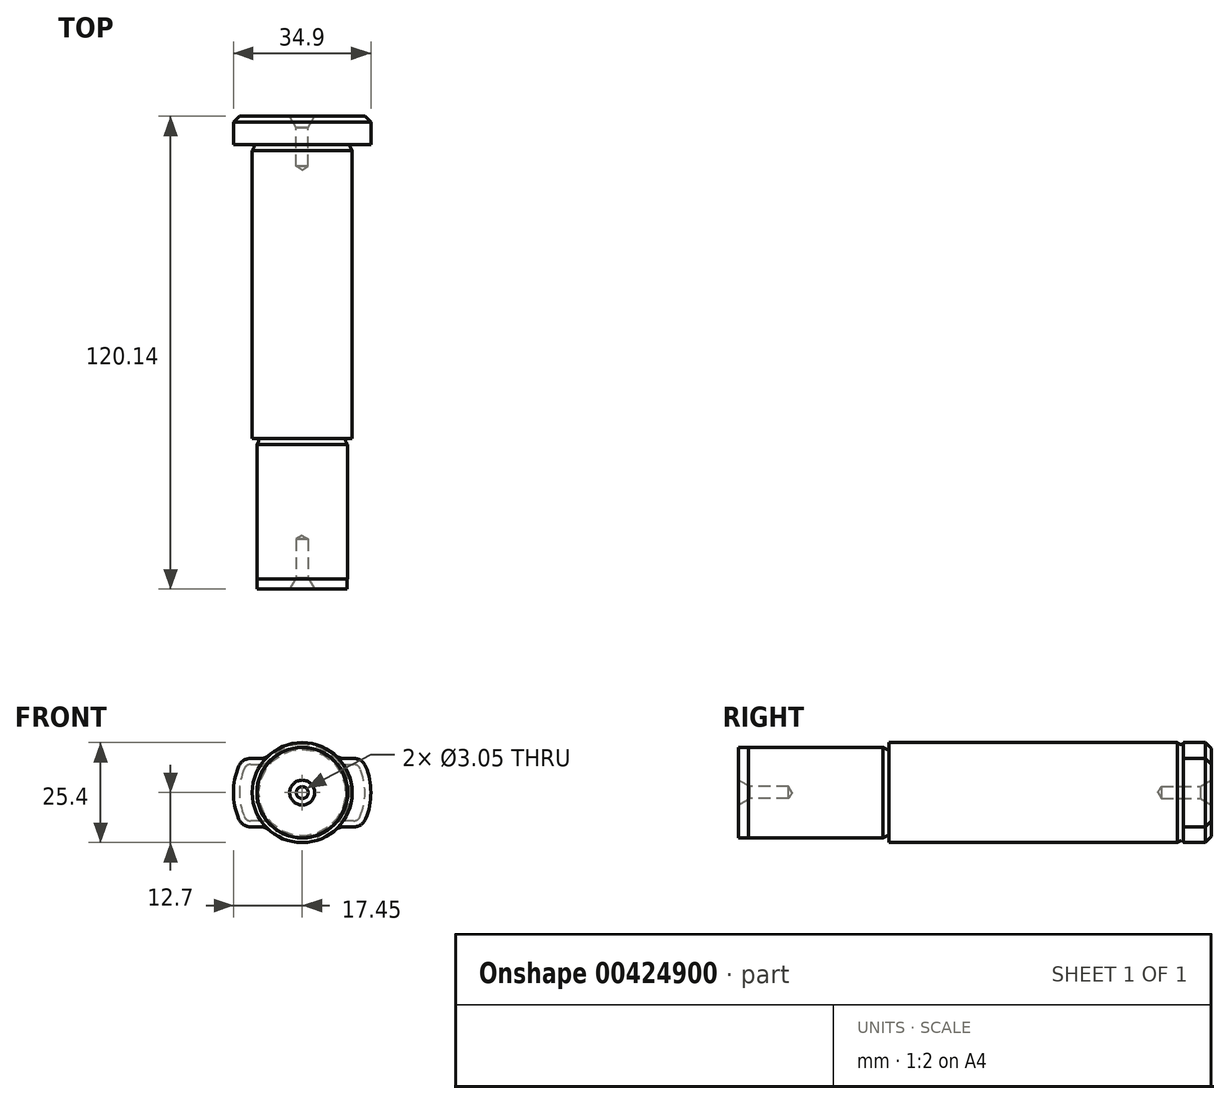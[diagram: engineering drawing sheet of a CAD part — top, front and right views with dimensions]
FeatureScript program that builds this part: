
annotation { "Feature Type Name" : "Feature", "Feature Type Description" : "" }
export const myFeature = defineFeature(function(context is Context, id is Id, definition is map)
    precondition{}
    {
        {
            var Q0;
            Q0=qCreatedBy(makeId("Front.planeOp"),FACE);
            var sketch = newSketch(context, id + "F0", { "sketchPlane" : qUnion([Q0])});
            skCircle(sketch, "E0", {"center": v(0, 0) * mm, "radius": 11.44 * mm});
            skSolve(sketch);
        }
        {
            var Q0;
            Q0 = qSketchRegion(id + "F0", true);
            extrude(context, id + "F1", {"entities" : qUnion([Q0]), "oppositeDirection" : true, "depth" : 2.54 * mm});
        }
        {
            var Q0;
            Q0=makeQuery(id+"F1.opExtrude","CAP_FACE",FACE,{"disambiguationData":[OSD([sQuery(id+"F0.wireOp",EDGE,"E0")])],"isStart":false});
            var sketch = newSketch(context, id + "F2", { "sketchPlane" : qUnion([Q0])});
            skCircle(sketch, "E1", {"center": v(0, 0) * mm, "radius": 11.52 * mm});
            skSolve(sketch);
        }
        {
            var Q0;
            Q0 = qSketchRegion(id + "F2", true);
            extrude(context, id + "F3", {"entities" : qUnion([Q0]), "operationType" : NewBodyOperationType.ADD, "depth" : 35.74 * mm});
        }
        {
            var Q0;
            Q0=makeQuery(id+"F3.opExtrude","CAP_FACE",FACE,{"disambiguationData":[OSD([sQuery(id+"F2.wireOp",EDGE,"E1")])],"isStart":false});
            var sketch = newSketch(context, id + "F4", { "sketchPlane" : qUnion([Q0])});
            skCircle(sketch, "E2", {"center": v(0, 0) * mm, "radius": 12.7 * mm});
            skSolve(sketch);
        }
        {
            var Q0;
            Q0=makeQuery(id+"F4.imprint","IMPRINT",FACE,{"disambiguationData":[TD([[makeQuery(id+"F4.imprint","IMPRINT",EDGE,{"derivedFrom":makeQuery(id+"F3.opExtrude","CAP_EDGE",EDGE,{"disambiguationData":[OSD([sQuery(id+"F2.wireOp",EDGE,"E1")])],"isStart":false})}),1.0]])]});
            var Q1;
            Q1=makeQuery(id+"F4.imprint","IMPRINT",FACE,{"disambiguationData":[TD([[makeQuery(id+"F4.imprint","IMPRINT",EDGE,{"derivedFrom":sQuery(id+"F4.wireOp",EDGE,"E2")}),1.0]])]});
            extrude(context, id + "F5", {"entities" : qUnion([Q0, Q1]), "operationType" : NewBodyOperationType.ADD, "depth" : 74.73 * mm});
        }
        {
            var Q0;
            Q0=makeQuery(id+"F5.opExtrude","CAP_FACE",FACE,{"disambiguationData":[OSD([sQuery(id+"F4.wireOp",EDGE,"E2")])],"isStart":false});
            var sketch = newSketch(context, id + "F6", { "sketchPlane" : qUnion([Q0])});
            skLineSegment(sketch, "E3.bottom", {"start": v(15.13, 8.7) * mm, "end": v(9.25, 8.7) * mm});
            skLineSegment(sketch, "E3.top", {"start": v(15.13, -8.7) * mm, "end": v(9.25, -8.7) * mm});
            skArc(sketch, "E4", {"start": v(15.13, 8.7) * mm, "mid": v(17.45, 0) * mm, "end": v(15.13, -8.7) * mm});
            skArc(sketch, "E5", {"start": v(-15.13, 8.7) * mm, "mid": v(-17.45, 0) * mm, "end": v(-15.13, -8.7) * mm});
            skArc(sketch, "E6.0", {"start": v(-9.25, -8.7) * mm, "mid": v(0, -12.7) * mm, "end": v(9.25, -8.7) * mm});
            skLineSegment(sketch, "E7.trimOffspring", {"start": v(-9.25, 8.7) * mm, "end": v(-15.13, 8.7) * mm});
            skLineSegment(sketch, "E8.trimOffspring", {"start": v(-9.25, -8.7) * mm, "end": v(-15.13, -8.7) * mm});
            skArc(sketch, "E9.trimOffspring", {"start": v(9.25, 8.7) * mm, "mid": v(0, 12.7) * mm, "end": v(-9.25, 8.7) * mm});
            skSolve(sketch);
        }
        {
            var Q0;
            {var subQ0=sQuery(id+"F6.wireOp",EDGE,"E6.0");Q0=makeQuery(id+"F6.imprint","IMPRINT",FACE,{"disambiguationData":[TD([[makeQuery(id+"F6.imprint","IMPRINT",EDGE,{"derivedFrom":subQ0}),1.0]])]});}
            var Q1;
            {var subQ0=sQuery(id+"F6.wireOp",EDGE,"E3.bottom");Q1=makeQuery(id+"F6.imprint","IMPRINT",FACE,{"disambiguationData":[TD([[makeQuery(id+"F6.imprint","IMPRINT",EDGE,{"derivedFrom":subQ0}),1.0]])]});}
            var Q2;
            Q2=makeQuery(id+"F6.imprint","IMPRINT",FACE,{"disambiguationData":[TD([[makeQuery(id+"F6.imprint","IMPRINT",EDGE,{"derivedFrom":sQuery(id+"F6.wireOp",EDGE,"E5")}),1.0]])]});
            extrude(context, id + "F7", {"entities" : qUnion([Q0, Q1, Q2]), "operationType" : NewBodyOperationType.ADD, "depth" : 7.14 * mm});
        }
        {
            var Q0;
            Q0=makeQuery(id+"F7.opExtrude","SWEPT_EDGE",EDGE,{"disambiguationData":[OSD([sQuery(id+"F6.wireOp",EDGE,"E3.top"),sQuery(id+"F6.wireOp",EDGE,"E4")])]});
            var Q1;
            Q1=makeQuery(id+"F7.opExtrude","SWEPT_EDGE",EDGE,{"disambiguationData":[OSD([sQuery(id+"F4.wireOp",EDGE,"E2"),sQuery(id+"F6.wireOp",EDGE,"E3.top"),sQuery(id+"F6.wireOp",EDGE,"E6.0")])]});
            var Q2;
            Q2=makeQuery(id+"F7.opExtrude","SWEPT_EDGE",EDGE,{"disambiguationData":[OSD([sQuery(id+"F4.wireOp",EDGE,"E2"),sQuery(id+"F6.wireOp",EDGE,"E6.0"),sQuery(id+"F6.wireOp",EDGE,"E8.trimOffspring")])]});
            var Q3;
            Q3=makeQuery(id+"F7.opExtrude","SWEPT_EDGE",EDGE,{"disambiguationData":[OSD([sQuery(id+"F6.wireOp",EDGE,"E5"),sQuery(id+"F6.wireOp",EDGE,"E8.trimOffspring")])]});
            var Q4;
            Q4=makeQuery(id+"F7.opExtrude","SWEPT_EDGE",EDGE,{"disambiguationData":[OSD([sQuery(id+"F6.wireOp",EDGE,"E3.bottom"),sQuery(id+"F6.wireOp",EDGE,"E4")])]});
            var Q5;
            Q5=makeQuery(id+"F7.opExtrude","SWEPT_EDGE",EDGE,{"disambiguationData":[OSD([sQuery(id+"F4.wireOp",EDGE,"E2"),sQuery(id+"F6.wireOp",EDGE,"E3.bottom"),sQuery(id+"F6.wireOp",EDGE,"E9.trimOffspring")])]});
            var Q6;
            Q6=makeQuery(id+"F7.opExtrude","SWEPT_EDGE",EDGE,{"disambiguationData":[OSD([sQuery(id+"F4.wireOp",EDGE,"E2"),sQuery(id+"F6.wireOp",EDGE,"E7.trimOffspring"),sQuery(id+"F6.wireOp",EDGE,"E9.trimOffspring")])]});
            var Q7;
            Q7=makeQuery(id+"F7.opExtrude","SWEPT_EDGE",EDGE,{"disambiguationData":[OSD([sQuery(id+"F6.wireOp",EDGE,"E5"),sQuery(id+"F6.wireOp",EDGE,"E7.trimOffspring")])]});
            fillet(context, id + "F8", {"entities" : qUnion([Q0, Q1, Q2, Q3, Q4, Q5, Q6, Q7]), "radius" : 3.3 * mm, "tangentPropagation" : true, "allowEdgeOverflow" : false});
        }
        {
            var Q0;
            Q0=makeQuery(id+"F7.opExtrude","CAP_EDGE",EDGE,{"disambiguationData":[OSD([sQuery(id+"F6.wireOp",EDGE,"E9.trimOffspring")])],"isStart":false});
            chamfer(context, id + "F9", {"entities" : qUnion([Q0]), "width" : 1.52 * mm, "tangentPropagation" : true});
        }
        {
            var Q0;
            Q0=qCreatedBy(makeId("Top.planeOp"),FACE);
            var sketch = newSketch(context, id + "F10", { "sketchPlane" : qUnion([Q0])});
            skLineSegment(sketch, "E10", {"start": v(-12.7, 38.28) * mm, "end": v(-12.7, 113) * mm});
            skLineSegment(sketch, "E11", {"start": v(12.7, 113) * mm, "end": v(12.7, 38.28) * mm});
            skLineSegment(sketch, "E12.0.0", {"start": v(-16.13, 113) * mm, "end": v(-17.45, 113) * mm});
            skLineSegment(sketch, "E12.0.1", {"start": v(-16.13, 113) * mm, "end": v(-13.08, 113) * mm});
            skLineSegment(sketch, "E12.0.2", {"start": v(-13.08, 113) * mm, "end": v(-10.58, 113) * mm});
            skLineSegment(sketch, "E12.0.3", {"start": v(-10.58, 113) * mm, "end": v(-8.4, 113) * mm});
            skLineSegment(sketch, "E12.0.4", {"start": v(-8.4, 113) * mm, "end": v(-12.7, 113) * mm});
            skLineSegment(sketch, "E12.0.5", {"start": v(-8.4, 113) * mm, "end": v(-10.58, 113) * mm});
            skLineSegment(sketch, "E12.0.6", {"start": v(-10.58, 113) * mm, "end": v(-13.08, 113) * mm});
            skLineSegment(sketch, "E12.0.7", {"start": v(-13.08, 113) * mm, "end": v(-16.13, 113) * mm});
            skLineSegment(sketch, "E13", {"start": v(-12.7, 111.48) * mm, "end": v(-12.26, 112.24) * mm});
            skArc(sketch, "E14", {"start": v(-12.26, 112.24) * mm, "mid": v(-12.26, 112.75) * mm, "end": v(-12.7, 113) * mm});
            skLineSegment(sketch, "E15", {"start": v(0, 0) * mm, "end": v(0, 64.08) * mm});
            skLineSegment(sketch, "E16", {"start": v(-11.52, 2.54) * mm, "end": v(-11.52, 38.28) * mm});
            skLineSegment(sketch, "E17", {"start": v(11.52, 38.28) * mm, "end": v(11.52, 2.54) * mm});
            skLineSegment(sketch, "E18.0.0", {"start": v(12.7, 38.28) * mm, "end": v(-12.7, 38.28) * mm});
            skLineSegment(sketch, "E19", {"start": v(-11.52, 30.63) * mm, "end": v(-9.02, 34.97) * mm});
            skArc(sketch, "E20", {"start": v(-9.02, 34.97) * mm, "mid": v(-9.3, 37.69) * mm, "end": v(-11.97, 38.28) * mm});
            skArc(sketch, "E21", {"start": v(-11.97, 38.28) * mm, "mid": v(-11.4, 35.5) * mm, "end": v(-10.82, 38.28) * mm});
            skLineSegment(sketch, "E22", {"start": v(11.52, 36.75) * mm, "end": v(11.08, 37.52) * mm});
            skArc(sketch, "E23", {"start": v(11.08, 37.52) * mm, "mid": v(11.08, 38.02) * mm, "end": v(11.52, 38.28) * mm});
            skSolve(sketch);
        }
        {
            var Q0;
            {var subQ2=sQuery(id+"F10.wireOp",EDGE,"E13");Q0=makeQuery(id+"F10.imprint","IMPRINT",FACE,{"disambiguationData":[TD([[makeQuery(id+"F10.imprint","IMPRINT",EDGE,{"derivedFrom":subQ2}),1.0]])]});}
            var Q1;
            {var subQ2=sQuery(id+"F10.wireOp",EDGE,"E22");Q1=makeQuery(id+"F10.imprint","IMPRINT",FACE,{"disambiguationData":[TD([[makeQuery(id+"F10.imprint","IMPRINT",EDGE,{"derivedFrom":subQ2}),-1.0]])]});}
            var Q2;
            Q2=sQuery(id+"F10.wireOp",EDGE,"E15");
            revolve(context, id + "F11", {"operationType" : NewBodyOperationType.REMOVE, "entities" : qUnion([Q0, Q1]), "axis" : qUnion([Q2]), "revolveType" : RevolveType.FULL, "oppositeDirection" : true});
        }
        {
            var Q0;
            Q0=makeQuery(id+"F1.opExtrude","CAP_FACE",FACE,{"disambiguationData":[OSD([sQuery(id+"F0.wireOp",EDGE,"E0")])],"isStart":true});
            var sketch = newSketch(context, id + "F12", { "sketchPlane" : qUnion([Q0])});
            skPoint(sketch, "E24", {"position": v(0, 0) * mm});
            skSolve(sketch);
        }
        {
            var Q0;
            Q0=sQuery(id+"F12.wireOp",VERTEX,"E24");
            var Q1;
            Q1=makeQuery(id+"F1.opExtrude","SWEPT_BODY",BODY,{"disambiguationData":[OSD([sQuery(id+"F0.wireOp",EDGE,"E0")])]});
            hole(context, id + "F13", {"style" : HoleStyle.C_SINK, "endStyle" : HoleEndStyle.BLIND, "holeDiameter" : 3.05 * mm, "cSinkDiameter" : 6.35 * mm, "cSinkAngle" : 60 * degree, "holeDepth" : 12.7 * mm, "isTappedThrough" : true, "tappedDepth" : 12.7 * mm, "tapClearance" : 3, "locations" : qUnion([Q0]), "scope" : qUnion([Q1])});
        }
        {
            var Q0;
            Q0=makeQuery(id+"F7.opExtrude","CAP_FACE",FACE,{"disambiguationData":[OSD([sQuery(id+"F6.wireOp",EDGE,"E3.bottom"),sQuery(id+"F6.wireOp",EDGE,"E3.top"),sQuery(id+"F6.wireOp",EDGE,"E4"),sQuery(id+"F6.wireOp",EDGE,"E5"),sQuery(id+"F6.wireOp",EDGE,"E6.0"),sQuery(id+"F6.wireOp",EDGE,"E7.trimOffspring"),sQuery(id+"F6.wireOp",EDGE,"E8.trimOffspring"),sQuery(id+"F6.wireOp",EDGE,"E9.trimOffspring")])],"isStart":false});
            var sketch = newSketch(context, id + "F14", { "sketchPlane" : qUnion([Q0])});
            skPoint(sketch, "E25", {"position": v(0, 0) * mm});
            skSolve(sketch);
        }
        {
            var Q0;
            Q0=sQuery(id+"F14.wireOp",VERTEX,"E25");
            var Q1;
            Q1=makeQuery(id+"F1.opExtrude","SWEPT_BODY",BODY,{"disambiguationData":[OSD([sQuery(id+"F0.wireOp",EDGE,"E0")])]});
            hole(context, id + "F15", {"style" : HoleStyle.C_SINK, "endStyle" : HoleEndStyle.BLIND, "holeDiameter" : 3.05 * mm, "cSinkDiameter" : 6.35 * mm, "cSinkAngle" : 60 * degree, "holeDepth" : 12.7 * mm, "isTappedThrough" : true, "tappedDepth" : 12.7 * mm, "tapClearance" : 3, "locations" : qUnion([Q0]), "scope" : qUnion([Q1])});
        }
    });
